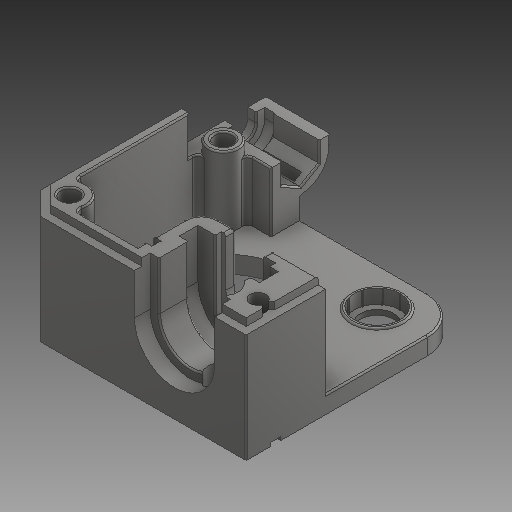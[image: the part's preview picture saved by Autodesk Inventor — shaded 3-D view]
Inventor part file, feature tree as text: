
AUTODESK INVENTOR PART (.ipt)
format: ipt  version: 2018 (Build 220112000, 112)  size: 1,065,984 bytes
history: native  units: in
note: dims shown in document units (in); Inventor stores cm internally (conversion verified against a paired STEP export)
features: extrude x35, sketch x35, projected_geometry x24, fillet x7, chamfer x3, pattern_circular x1
ambient origin geometry x8: Origin, YZ Plane, XZ Plane, XY Plane, X Axis, Y Axis, Z Axis, Center Point
bodies: Solid1 (feature_tree)
feature tree (105):
  extrude  "Extrusion1"  Depth=1.811in
  fillet  "Fillet1"  Radius=1.7323in
  extrude  "Extrusion2"  Depth=0.815in
  extrude  "Extrusion3"  Depth=0.2953in
  extrude  "Extrusion4"  Depth=1.2205in
  fillet  "Fillet2"  Radius=0.1437in
  extrude  "Extrusion5"  Depth=0.1437in
  fillet  "Fillet3"  Radius=0.2638in
  pattern_circular  "Circular Pattern1"  Count=10 Angle=360.0deg
  extrude  "Extrusion6"  Depth=0.1181in
  extrude  "Extrusion7"  Depth=0.6299in
  extrude  "Extrusion8"  Depth=0.7835in TaperAngle=0.0deg
  extrude  "Extrusion9"  TaperAngle=0.0deg  [1 undecoded]
  extrude  "Extrusion10"  Depth=1.2402in
  extrude  "Extrusion11"  Depth=0.1831in
  extrude  "Extrusion12"  Depth=0.0689in TaperAngle=0.0deg
  extrude  "Extrusion13"  Depth=0.0787in TaperAngle=0.0deg
  extrude  "Extrusion14"  Depth=0.0787in TaperAngle=0.0deg
  extrude  "Extrusion15"  Depth=0.0591in
  extrude  "Extrusion16"  Depth=0.2441in
  extrude  "Extrusion17"  TaperAngle=0.0deg  [1 undecoded]
  extrude  "Extrusion18"  Depth=0.5551in
  extrude  "Extrusion19"  Depth=0.6378in
  extrude  "Extrusion20"  Depth=0.5354in
  extrude  "Extrusion21"  Depth=0.2303in TaperAngle=0.0deg
  extrude  "Extrusion22"  Depth=0.0709in
  chamfer  "Chamfer1"  Distance=0.0492in
  extrude  "Extrusion23"  Depth=0.0492in TaperAngle=0.0deg
  extrude  "Extrusion24"  Depth=0.0492in TaperAngle=0.0deg
  extrude  "Extrusion25"  Depth=0.0787in TaperAngle=0.0deg
  fillet  "Fillet4"  Radius=0.0591in
  chamfer  "Chamfer2"  Distance=0.0591in
  extrude  "Extrusion26"  Depth=0.0787in
  fillet  "Fillet6"  Radius=0.5512in
  fillet  "Fillet7"  Radius=0.0591in
  fillet  "Fillet8"  Radius=0.0492in
  extrude  "Extrusion27"  Depth=0.0787in TaperAngle=0.0deg
  extrude  "Extrusion28"  Depth=0.0787in TaperAngle=0.0deg
  extrude  "Extrusion29"  Depth=0.0787in
  extrude  "Extrusion30"  Depth=0.0787in TaperAngle=45.0deg
  extrude  "Extrusion31"  Depth=0.0591in
  extrude  "Extrusion32"  Depth=0.0591in
  extrude  "Extrusion33"  Depth=0.0591in
  extrude  "Extrusion34"  Depth=0.0591in
  extrude  "Extrusion35"  Depth=0.0591in TaperAngle=0.0deg
  chamfer  "Chamfer3"  Distance=0.0394in
  sketch  "Sketch1"  dims[d0=1.063in d1=1.811in d2=1.7323in]
  sketch  "Sketch2"  dims[d3=0.815in d4=0.815in]
  sketch  "Sketch3"  dims[d5=0.1378in d6=0.0in d7=0.2953in]
  projected_geometry  "Projected Loop1"
  sketch  "Sketch4"  dims[d8=1.2205in d9=1.2205in d10=0.1437in]
  projected_geometry  "Projected Loop2"
  sketch  "Sketch5"  dims[d11=0.1437in d12=0.1437in d13=0.2638in]
  projected_geometry  "Projected Loop3"
  sketch  "Sketch7"  dims[d14=0.1378in d15=0.0in]
  projected_geometry  "Projected Loop4"
  sketch  "Sketch8"  dims[d16=0.3622in]
  sketch  "Sketch9"  dims[d17=0.0984in d18=0.0in]
  sketch  "Sketch10"  dims[d19=0.4173in]
  sketch  "Sketch11"  dims[d20=0.0138in d21=0.0in]
  projected_geometry  "Projected Loop5"
  sketch  "Sketch13"  dims[d22=0.0138in]
  projected_geometry  "Projected Loop7"
  sketch  "Sketch14"  dims[d23=0.0118in]
  projected_geometry  "Projected Loop8"
  sketch  "Sketch15"  dims[d24=0.1752in]
  sketch  "Sketch16"  dims[d25=0.0138in d26=0.0in]
  projected_geometry  "Projected Loop9"
  sketch  "Sketch17"  dims[d27=0.0059in d28=3.937in d29=360.0deg]
  projected_geometry  "Projected Loop10"
  sketch  "Sketch18"  dims[d31=0.5118in d33=0.1181in]
  projected_geometry  "Projected Loop11"
  sketch  "Sketch19"  dims[d34=0.9843in d35=0.6299in]
  projected_geometry  "Projected Loop12"
  sketch  "Sketch21"  dims[d36=0.1181in d37=0.7835in d38=0.0in]
  sketch  "Sketch22"  dims[d42=0.5354in d43=0.0in d44=0.0in]
  projected_geometry  "Projected Loop14"
  sketch  "Sketch23"  dims[d46=0.6102in d47=1.2402in]
  projected_geometry  "Projected Loop15"
  sketch  "Sketch24"  dims[d48=0.9213in d49=0.0in d50=0.1831in]
  sketch  "Sketch25"  dims[d51=0.0915in d52=0.0689in d53=0.0in]
  projected_geometry  "Projected Loop16"
  sketch  "Sketch26"  dims[d54=0.315in d55=0.0787in d56=0.0in]
  projected_geometry  "Projected Loop17"
  sketch  "Sketch27"  dims[d57=0.2972in d58=0.0787in d59=0.0in]
  projected_geometry  "Projected Loop18"
  sketch  "Sketch28"  dims[d60=0.0591in d62=0.0394in]
  projected_geometry  "Projected Loop19"
  sketch  "Sketch29"  dims[d63=0.0669in d64=0.0in d65=0.2441in]
  projected_geometry  "Projected Loop20"
  projected_geometry  "Projected Loop21"
  sketch  "Sketch30"  dims[d66=0.5551in d67=0.0in]
  sketch  "Sketch31"  dims[d68=0.0689in d69=0.5551in]
  sketch  "Sketch32"  dims[d70=0.0in d72=0.6378in]
  projected_geometry  "Projected Loop22"
  sketch  "Sketch33"  dims[d73=0.248in d74=0.5354in]
  projected_geometry  "Projected Loop23"
  sketch  "Sketch34"  dims[d75=0.124in d76=0.0in d78=0.2303in d79=0.0in]
  sketch  "Sketch35"  dims[d80=0.1496in d81=0.0in d82=0.0709in d83=0.0492in d84=0.0in]
  sketch  "Sketch36"  dims[d85=0.2953in d86=0.0492in d87=0.0in]
  projected_geometry  "Projected Loop24"
  sketch  "Sketch37"  dims[d88=0.2362in d89=0.0492in d90=0.0in]
  projected_geometry  "Projected Loop25"
  sketch  "Sketch38"  dims[d91=0.2362in d92=0.0492in d93=0.0in d94=0.0591in d95=0.0591in d97=0.0728in d98=0.5512in d99=0.0in d100=0.0591in d101=0.0787in d102=45.0deg d103=0.0492in d104=0.0in d105=0.0492in d106=0.0in d107=0.0079in d108=0.0in d109=0.1378in d110=0.1772in d111=0.0787in d112=45.0deg d113=0.0591in d114=0.0591in d115=0.0591in d116=0.0591in d117=0.0591in d118=0.0in d120=0.0394in d121=0.0118in d122=0.0197in d123=0.3425in d124=0.0925in d125=0.0866in d126=0.0669in d127=0.3307in d128=0.0in d129=0.0551in d130=0.1575in d131=0.0787in d132=0.0531in d133=0.1575in d134=0.3445in d135=0.1575in d136=0.0in d137=0.5512in d138=0.1575in d139=0.0in d140=0.1575in d141=0.0in d142=0.0984in d143=0.0394in d144=0.1575in d145=0.0in d146=0.126in d147=0.2362in d148=0.1417in d149=0.0531in d150=0.1575in d151=0.0in d152=0.1575in d153=0.0in d154=0.2126in d155=0.0787in d156=0.0276in d157=0.0in d158=0.1575in d159=0.1181in d160=0.0in d161=0.863in d162=0.0236in d163=0.0787in d164=45.0deg]
  projected_geometry  "Projected Loop26"
note: 2 required parameter values undecoded (feature->parameter linkage not recoverable at this tier; creation-order binding heuristic only, values carry confidence <= 0.55)
